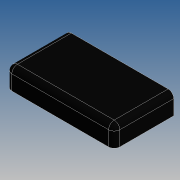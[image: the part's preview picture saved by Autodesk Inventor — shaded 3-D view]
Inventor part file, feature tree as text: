
AUTODESK INVENTOR PART (.ipt)
format: ipt  version: 2019 (Build 230136000, 136)  size: 287,744 bytes
history: native  units: mm
features: extrude x3, fillet x3, sketch x3, shell x1, chamfer x1, mirror x1, projected_geometry x1
ambient origin geometry x8: Origin, YZ Plane, XZ Plane, XY Plane, X Axis, Y Axis, Z Axis, Center Point
bodies: Solid1 (feature_tree)
feature tree (13):
  extrude  "Extrusion1"  Depth=32.0mm
  fillet  "Fillet1"  Radius=11.0mm
  fillet  "Fillet2"  Radius=2.0mm
  shell  "Shell1"  Thickness=3.0mm
  extrude  "Extrusion3"  Depth=1.0mm
  extrude  "Extrusion4"  Depth=0.2mm
  chamfer  "Chamfer2"  Distance=0.2mm
  fillet  "Fillet4"  Radius=0.2mm
  mirror  "Mirror1"
  sketch  "Sketch1"  dims[d0=29.0mm d1=32.0mm d2=11.0mm d3=0.0mm d4=2.0mm d5=3.0mm]
  sketch  "Sketch3"  dims[d6=3.0mm d19=1.0mm]
  sketch  "Sketch4"  dims[d20=2.0mm d21=0.0mm d22=5.0mm d23=0.2mm d24=0.2mm d25=10.0mm d26=10.0mm d27=3.0mm d28=0.4mm d29=0.8mm d30=0.0mm d32=0.4mm d33=2.0mm d34=45.0deg d35=0.2mm]
  projected_geometry  "Project Cut Edges1"
